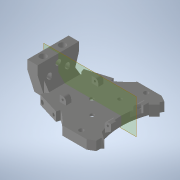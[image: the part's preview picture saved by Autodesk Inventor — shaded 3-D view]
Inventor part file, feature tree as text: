
AUTODESK INVENTOR PART (.ipt)
format: ipt  version: 2022 (Build 260153000, 153)  size: 543,232 bytes
history: native  units: mm
features: extrude x15, sketch x14, reference x8, other x8, plane x7, chamfer x6, mirror x3, projected_geometry x2, pattern_circular x1, fillet x1
ambient origin geometry x8: Origin, YZ Plane, XZ Plane, XY Plane, X Axis, Y Axis, Z Axis, Center Point
bodies: Solid1 (feature_tree)
feature tree (65):
  extrude  "Extrusion1"  Depth=13.0mm
  extrude  "Extrusion2"  Depth=9.0mm
  pattern_circular  "Circular Pattern1"  Count=3 Angle=360.0deg
  extrude  "Extrusion6"  Depth=7.0mm TaperAngle=0.0deg
  plane  "Work Plane1"
  plane  "Work Plane4"
  extrude  "Extrusion10"  Depth=15.0mm
  chamfer  "Chamfer3"  Distance=24.25mm
  extrude  "Extrusion11"  Depth=4.0mm
  chamfer  "Chamfer4"  Distance=30.0mm
  plane  "Work Plane5"
  plane  "Work Plane6"
  plane  "Work Plane7"
  extrude  "Extrusion15"  Depth=8.0mm
  extrude  "Extrusion16"  Depth=8.0mm
  mirror  "Mirror1"
  extrude  "Extrusion17"  Depth=8.0mm
  chamfer  "Chamfer5"  Distance=68.718732mm
  chamfer  "Chamfer6"  Distance=3.5mm
  extrude  "Extrusion19"  Depth=3.425mm TaperAngle=0.0deg
  mirror  "Mirror2"
  plane  "Work Plane3"
  extrude  "Extrusion20"  [1 undecoded]
  fillet  "Fillet4"  Radius=4.0mm
  mirror  "Mirror3"
  extrude  "Extrusion21"  Depth=8.0mm
  chamfer  "Chamfer7"  [1 undecoded]
  extrude  "Extrusion22"  TaperAngle=0.0deg  [1 undecoded]
  extrude  "Extrusion23"  Depth=8.0mm
  chamfer  "Chamfer9"  Distance=12.0mm
  extrude  "Extrusion24"  Depth=8.0mm TaperAngle=0.0deg
  extrude  "Extrusion25"  Depth=8.0mm
  sketch  "Sketch1"  dims[d0=25.8mm d1=13.0mm]
  sketch  "Sketch2"  dims[d2=15.0mm d3=9.0mm]
  sketch  "Sketch6"  dims[d4=8.0mm]
  reference  "Reference1"
  sketch  "Sketch11"  dims[d5=5.0mm]
  projected_geometry  "Projected Loop8"
  sketch  "Sketch15"  dims[d6=25.0mm]
  sketch  "Sketch16"  dims[d7=4.0mm d8=30.0mm d10=360.0deg]
  plane  "Work Plane2"
  sketch  "Sketch17"  dims[d12=30.0mm d14=360.0deg d16=7.0mm d17=0.0mm]
  reference  "Reference6"
  sketch  "Sketch20"  dims[d18=13.0mm d19=15.0mm]
  reference  "Reference7"
  sketch  "Sketch21"  dims[d20=9.0mm]
  reference  "Reference8"
  reference  "Reference9"
  sketch  "Sketch22"  dims[d21=8.0mm]
  sketch  "Sketch23"  dims[d22=5.0mm d24=24.25mm d25=0.0mm]
  sketch  "Sketch24"  dims[d41=30.0mm d42=360.0deg d52=4.0mm]
  sketch  "Sketch25"  dims[d53=4.0mm]
  reference  "Reference10"
  sketch  "Sketch26"  dims[d54=15.0mm d55=30.0mm d56=4.0mm d57=4.0mm d58=68.718732mm d59=68.718732mm d60=3.5mm d61=3.425mm d62=0.0mm d63=-15.0mm d95=4.0mm d96=4.0mm d99=0.0mm d100=0.0mm d101=12.0mm d103=12.0mm d104=8.0mm d105=0.0mm d106=4.2mm d107=6.0mm d108=2.0mm d109=45.0deg d110=0.1mm d111=0.0mm d112=5.0mm d113=2.0mm d114=45.0deg d123=4.0mm d124=4.0mm d125=4.0mm d126=4.0mm d127=10.0mm d128=0.0mm d131=7.0mm d132=0.0mm d135=18.5mm d136=3.0mm d137=2.96706mm d138=0.0mm d139=4.0mm d140=4.0mm d141=7.0mm d142=0.0mm d148=8.0mm d149=0.0mm d150=0.0mm d151=6.0mm d152=45.0deg d153=4.0mm d154=45.0deg d155=1.3mm d156=6.0mm d157=45.0deg d158=1.3mm d159=6.0mm d160=45.0deg d163=2.5mm d164=0.2mm d165=8.0mm d166=0.0mm d167=-14.615mm d168=4.0mm d169=0.0mm d170=2.0mm d171=7.5mm d172=0.0mm d174=1.8mm d175=1.8mm d176=4.0mm d177=2.0mm d178=45.0deg d180=3.0mm d181=3.0mm d182=10.75mm d183=0.0mm d184=11.0mm d185=7.0mm d186=0.0mm d190=46.0mm d191=28.5mm d192=9.0mm d193=10.0mm d194=10.0mm d195=8.0mm d196=8.0mm d197=8.0mm d198=7.0mm d199=0.0mm d200=2.5mm d201=2.0mm d202=45.0deg d203=10.75mm d204=0.0mm d205=5.2mm d206=5.2mm d207=8.0mm d208=0.0mm]
  projected_geometry  "Projected Loop13"
  reference  "Reference11"
  reference  "Reference12"
  other  "volcano tool_MIRROR.iam"
  other  "E3D-VOLCANO-1.75-MO:1"
  other  "D2HW_C202M:1"
  other  "4010 turbo fan v3:1"
  other  "AquaPrinthead.iam"
  other  "Waterblock:1"
  parser-record x1  (decoder bookkeeping rows leaked as tree rows — omitted from the tree; the rows remain in map.json)
  other  "v6_Clamp aqua V2:1"
note: 3 required parameter values undecoded (feature->parameter linkage not recoverable at this tier; creation-order binding heuristic only, values carry confidence <= 0.55)
note: 1 file-system path scrubbed to <path> (originals preserved in map.json)
